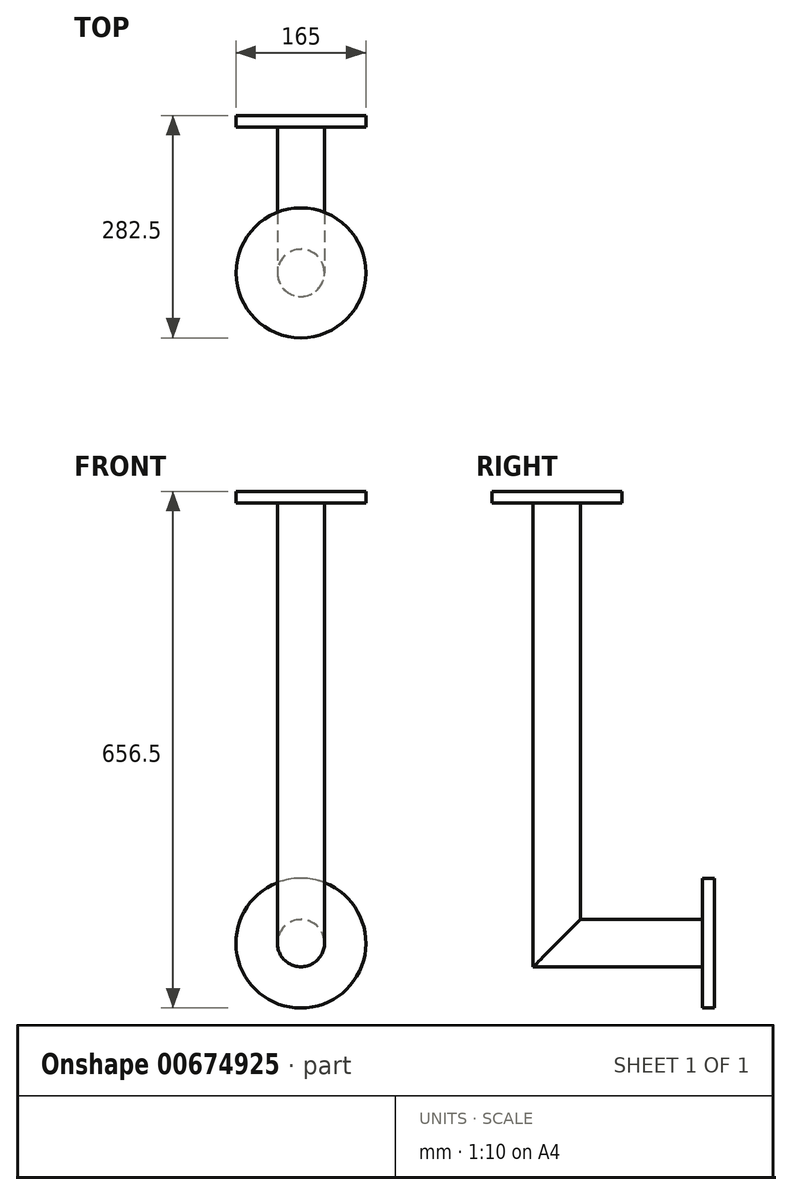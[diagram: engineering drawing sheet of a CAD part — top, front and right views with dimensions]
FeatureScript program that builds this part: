
annotation { "Feature Type Name" : "Feature", "Feature Type Description" : "" }
export const myFeature = defineFeature(function(context is Context, id is Id, definition is map)
    precondition{}
    {
        {
            var Q0;
            Q0=qCreatedBy(makeId("Front.planeOp"),FACE);
            var sketch = newSketch(context, id + "F0", { "sketchPlane" : qUnion([Q0])});
            skCircle(sketch, "E0", {"center": v(0, 0) * mm, "radius": 30 * mm});
            skCircle(sketch, "E1", {"center": v(0, 0) * mm, "radius": 82.5 * mm});
            skSolve(sketch);
        }
        {
            var Q0;
            Q0=qCreatedBy(makeId("Right.planeOp"),FACE);
            var sketch = newSketch(context, id + "F1", { "sketchPlane" : qUnion([Q0])});
            skLineSegment(sketch, "E2", {"start": v(0, 0) * mm, "end": v(-200, 0) * mm});
            skLineSegment(sketch, "E3", {"start": v(-200, 0) * mm, "end": v(-200, 574) * mm});
            skSolve(sketch);
        }
        {
            var Q0;
            Q0=makeQuery(id+"F0.imprint","IMPRINT",FACE,{"disambiguationData":[TD([[makeQuery(id+"F0.imprint","IMPRINT",EDGE,{"derivedFrom":sQuery(id+"F0.wireOp",EDGE,"E0")}),1.0]])]});
            var Q1;
            Q1=sQuery(id+"F1.wireOp",EDGE,"E2");
            var Q2;
            Q2=sQuery(id+"F1.wireOp",EDGE,"E3");
            sweep(context, id + "F2", {"profiles" : qUnion([Q0]), "path" : qUnion([Q1, Q2])});
        }
        {
            var Q0;
            Q0=makeQuery(id+"F0.imprint","IMPRINT",FACE,{"disambiguationData":[TD([[makeQuery(id+"F0.imprint","IMPRINT",EDGE,{"derivedFrom":sQuery(id+"F0.wireOp",EDGE,"E0")}),-1.0]])]});
            extrude(context, id + "F3", {"entities" : qUnion([Q0]), "operationType" : NewBodyOperationType.ADD, "depth" : 15 * mm, "offsetDistance" : 25 * mm});
        }
        {
            var Q0;
            Q0=makeQuery(id+"F2.opSweep","CAP_FACE",FACE,{"disambiguationData":[OSD([sQuery(id+"F0.wireOp",EDGE,"E0"),sQuery(id+"F1.wireOp",VERTEX,"E3.end")])],"isStart":false});
            var sketch = newSketch(context, id + "F4", { "sketchPlane" : qUnion([Q0])});
            skCircle(sketch, "E4", {"center": v(0, -200) * mm, "radius": 82.5 * mm});
            skSolve(sketch);
        }
        {
            var Q0;
            Q0=makeQuery(id+"F4.imprint","IMPRINT",FACE,{"disambiguationData":[TD([[makeQuery(id+"F4.imprint","IMPRINT",EDGE,{"derivedFrom":sQuery(id+"F4.wireOp",EDGE,"E4")}),1.0]])]});
            extrude(context, id + "F5", {"entities" : qUnion([Q0]), "operationType" : NewBodyOperationType.ADD, "oppositeDirection" : true, "depth" : 15 * mm, "offsetDistance" : 25 * mm});
        }
    });
